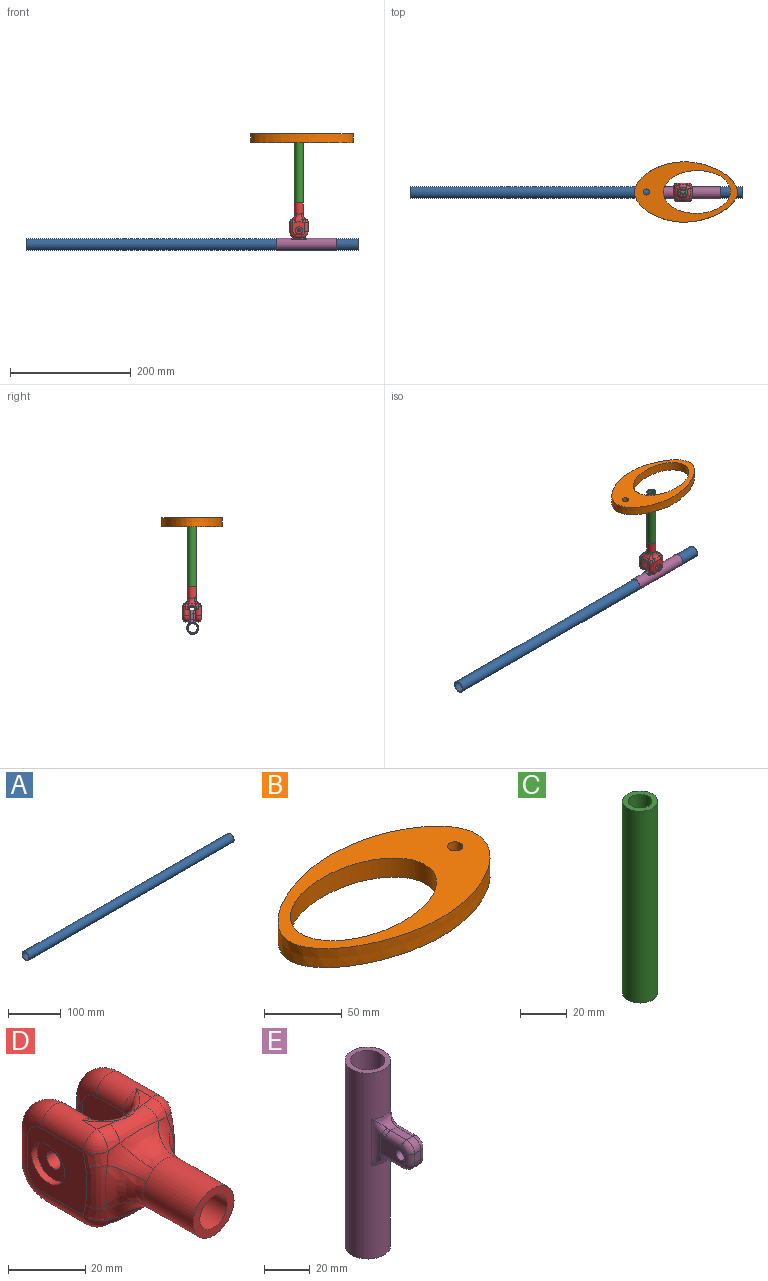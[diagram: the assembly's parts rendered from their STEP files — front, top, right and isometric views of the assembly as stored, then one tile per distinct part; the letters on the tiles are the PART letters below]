
ASSEMBLY  parts=5 mates=3
PART A: 4 faces, bbox 550x19x19 mm
  f0: cylinder r=8.5mm len=550mm, axis (-1,0,0), area 29373.9mm2, adj f2,f3
  f1: cylinder r=9.5mm len=550mm, axis (-1,0,0), area 32829.6mm2, adj f2,f3
  f2: plane 19x19mm, normal (1,0,0), area 56.5mm2, adj f0,f1
  f3: plane 19x19mm, normal (-1,0,0), area 56.5mm2, adj f0,f1
PART B: 5 faces, bbox 179.6x109.6x15 mm
  f0: extruded ~169.88x99.95mm, area 6393.3mm2, adj f1,f2
  f1: plane 179.64x109.64mm, normal (0,0,1), area 6702mm2, adj f0,f3,f4
  f2: plane 179.64x109.64mm, normal (0,0,-1), area 6702mm2, adj f0,f3,f4
  f3: extruded ~110.97x70.98mm, area 4340.2mm2, adj f1,f2
  f4: cylinder r=5mm len=15mm, axis (0,0,1), area 471.2mm2, adj f1,f2
PART C: 4 faces, bbox 15x15x100 mm
  f0: cylinder r=7.5mm len=100mm, axis (0,0,-1), area 4712.4mm2, adj f1,f2
  f1: plane 15x15mm, normal (0,0,1), area 98.2mm2, adj f0,f3
  f2: plane 15x15mm, normal (0,0,-1), area 98.2mm2, adj f0,f3
  f3: cylinder r=5mm len=100mm, axis (0,0,-1), area 3141.6mm2, adj f1,f2
PART D: 69 faces, bbox 33.5x59.8x50.3 mm
  f0: cylinder r=2.5mm len=8mm, axis (-1,0,0), area 125.7mm2, adj f9,f68
  f1: cylinder r=2.5mm len=8mm, axis (-1,0,0), area 125.7mm2, adj f10,f66
  f2: plane 8x7.58mm, normal (0,0,1), area 13.9mm2, adj f29,f40,f42,f64
  f3: plane 8x7.58mm, normal (0,0,-1), area 13.9mm2, adj f28,f37,f39,f58
  f4: plane 2.98x0.91mm, normal (0,1,0), area 0.9mm2, adj f46,f50,f62
  f5: plane 8x7.58mm, normal (0,0,1), area 13.9mm2, adj f24,f38,f40,f60
  f6: plane 8x7.58mm, normal (0,0,-1), area 13.9mm2, adj f23,f35,f37,f55
  f7: plane 21.69x20mm, normal (-1,0,0), area 300.7mm2, adj f23,f24,f25,f26,f27,f33,f34,f36
  f8: plane 21.69x20mm, normal (1,0,0), area 300.7mm2, adj f28,f29,f30,f31,f32,f41,f43,f44
  f9: plane 20x15mm, normal (-1,0,0), area 269.6mm2, adj f0,f28,f29,f30,f31,f32,f47,f49
  f10: plane 20x15mm, normal (1,0,0), area 269.6mm2, adj f1,f23,f24,f25,f26,f27,f47,f49
  f11: plane 2.98x0.91mm, normal (0,1,0), area 0.9mm2, adj f45,f48,f57
  f12: cylinder r=7.5mm len=18mm, axis (0,1,0), area 848.2mm2, adj f13,f14,f15,f16,f17,f18,f19,f20
  f13: plane 15x15mm, normal (0,-1,0), area 98.2mm2, adj f12,f22
  f14: bspline ~20.33x10.71mm, area 103.8mm2, adj f12,f15,f16,f34
  f15: torus R=17.5mm, axis (0,1,0), area 61.1mm2, adj f12,f14,f17,f33,f35
  f16: torus R=17.5mm, axis (0,1,0), area 61.1mm2, adj f12,f14,f18,f36,f38
  f17: bspline ~20.33x10.71mm, area 103.8mm2, adj f12,f15,f19,f37
  f18: bspline ~20.33x10.71mm, area 103.8mm2, adj f12,f16,f20,f40
  f19: torus R=17.5mm, axis (0,1,0), area 61.1mm2, adj f12,f17,f21,f39,f41
  f20: torus R=17.5mm, axis (0,1,0), area 61.1mm2, adj f12,f18,f21,f42,f44
  f21: bspline ~20.33x10.71mm, area 103.8mm2, adj f12,f19,f20,f43
  f22: cylinder r=5mm len=38mm, axis (0,-1,0), area 1193.8mm2, adj f13,f47,f49
  f23: cylinder r=5mm len=15.38mm, axis (0,-1,0), area 199.3mm2, adj f6,f7,f10,f25,f45,f51
  f24: cylinder r=5mm len=15.38mm, axis (0,1,0), area 199.3mm2, adj f5,f7,f10,f26,f46,f52
  f25: torus R=5mm, axis (-1,0,0), area 201.9mm2, adj f7,f10,f23,f27
  f26: torus R=5mm, axis (-1,0,0), area 201.9mm2, adj f7,f10,f24,f27
  f27: cylinder r=5mm len=10mm, axis (0,0,-1), area 157.1mm2, adj f7,f10,f25,f26
  f28: cylinder r=5mm len=15.38mm, axis (0,1,0), area 199.3mm2, adj f3,f8,f9,f30,f48,f53
  f29: cylinder r=5mm len=15.38mm, axis (0,-1,0), area 199.3mm2, adj f2,f8,f9,f31,f50,f54
  f30: torus R=5mm, axis (-1,0,0), area 201.9mm2, adj f8,f9,f28,f32
  f31: torus R=5mm, axis (-1,0,0), area 201.9mm2, adj f8,f9,f29,f32
  f32: cylinder r=5mm len=10mm, axis (0,0,1), area 157.1mm2, adj f8,f9,f30,f31
  f33: bspline ~8.9x6.01mm, area 25.9mm2, adj f7,f15,f34,f51
  f34: bspline ~14.38x4.87mm, area 72.5mm2, adj f7,f14,f33,f36
  f35: bspline ~8.9x6.01mm, area 25.9mm2, adj f6,f15,f37,f51
  f36: bspline ~8.9x6.01mm, area 25.9mm2, adj f7,f16,f34,f52
  f37: bspline ~14.38x4.87mm, area 70.7mm2, adj f3,f6,f17,f35,f39,f56,f57,f59
  f38: bspline ~8.9x6.01mm, area 25.9mm2, adj f5,f16,f40,f52
  f39: bspline ~8.9x6.01mm, area 25.9mm2, adj f3,f19,f37,f53
  f40: bspline ~14.43x4.88mm, area 70.7mm2, adj f2,f5,f18,f38,f42,f61,f62,f63
  f41: bspline ~8.9x6.01mm, area 25.9mm2, adj f8,f19,f43,f53
  f42: bspline ~8.9x6.01mm, area 25.9mm2, adj f2,f20,f40,f54
  f43: bspline ~14.43x4.88mm, area 72.5mm2, adj f8,f21,f41,f44
  f44: bspline ~8.9x6.01mm, area 25.9mm2, adj f8,f20,f43,f54
  f45: torus R=10mm, axis (0,-1,0), area 35.8mm2, adj f11,f23,f47,f55,f56
  f46: torus R=10mm, axis (0,-1,0), area 35.8mm2, adj f4,f24,f49,f60,f61
  f47: cylinder r=5mm len=10mm, axis (0,0,-1), area 107.1mm2, adj f9,f10,f22,f45,f48
  f48: torus R=10mm, axis (0,-1,0), area 35.8mm2, adj f11,f28,f47,f58,f59
  f49: cylinder r=5mm len=10mm, axis (0,0,-1), area 107.1mm2, adj f9,f10,f22,f46,f50
  f50: torus R=10mm, axis (0,-1,0), area 35.8mm2, adj f4,f29,f49,f63,f64
  f51: sphere r=5mm, area 50.9mm2, adj f23,f33,f35
  f52: sphere r=5mm, area 32.4mm2, adj f24,f36,f38
  f53: sphere r=5mm, area 32.4mm2, adj f28,f39,f41
  f54: sphere r=5mm, area 18.8mm2, adj f29,f42,f44
  f55: bspline ~7.97x6.73mm, area 9.8mm2, adj f6,f45,f56
  f56: bspline ~3.29x2.6mm, area 7mm2, adj f37,f45,f55,f57
  f57: bspline ~4.59x2.26mm, area 3.1mm2, adj f11,f37,f56,f59
  f58: bspline ~7.97x6.73mm, area 9.8mm2, adj f3,f48,f59
  f59: bspline ~3.29x2.6mm, area 7mm2, adj f37,f48,f57,f58
  f60: bspline ~7.97x6.73mm, area 9.8mm2, adj f5,f46,f61
  f61: bspline ~3.29x2.6mm, area 7mm2, adj f40,f46,f60,f62
  f62: bspline ~4.59x2.26mm, area 3.1mm2, adj f4,f40,f61,f63
  f63: bspline ~3.29x2.6mm, area 7mm2, adj f40,f50,f62,f64
  f64: bspline ~7.97x6.73mm, area 9.8mm2, adj f2,f50,f63
  f65: cylinder r=6mm len=12mm, axis (-1,0,0), area 75.4mm2, adj f7,f66
  f66: plane 12x12mm, normal (-1,0,0), area 93.5mm2, adj f1,f65
  f67: cylinder r=6mm len=12mm, axis (1,0,0), area 75.4mm2, adj f8,f68
  f68: plane 12x12mm, normal (1,0,0), area 93.5mm2, adj f0,f67
PART E: 34 faces, bbox 26.8x40x100 mm
  f0: cylinder r=10mm len=100mm, axis (0,0,-1), area 5916.2mm2, adj f1,f2,f8,f9,f10,f11
  f1: plane 20x20mm, normal (0,0,1), area 137.4mm2, adj f0,f14
  f2: plane 20x20mm, normal (0,0,-1), area 137.4mm2, adj f0,f14
  f3: plane 14.94x10.09mm, normal (-1,0,0), area 114.1mm2, adj f11,f16,f17,f18,f19,f20,f21,f22
  f4: plane 16.9x11.69mm, normal (1,0,0), area 134.6mm2, adj f8,f25,f26,f27,f28,f29,f30,f31
  f5: plane 10.32x4mm, normal (0,0,-1), area 40.3mm2, adj f10,f12,f17,f26
  f6: plane 10.32x4mm, normal (0,0,1), area 40.3mm2, adj f9,f13,f21,f30
  f7: plane 5x4mm, normal (0,-1,0), area 20mm2, adj f12,f13,f19,f28
  f8: cylinder r=5mm len=25mm, axis (0,0,-1), area 64.5mm2, adj f0,f4,f24,f32
  f9: torus R=15mm, axis (0,0,1), area 55.6mm2, adj f0,f6,f22,f23,f31,f32
  f10: torus R=15mm, axis (0,0,1), area 55.6mm2, adj f0,f5,f15,f16,f24,f25
  f11: cylinder r=5mm len=25mm, axis (0,0,-1), area 75.1mm2, adj f0,f3,f15,f23
  f12: cylinder r=5mm len=5mm, axis (-1,0,0), area 31.4mm2, adj f5,f7,f18,f27
  f13: cylinder r=5mm len=5mm, axis (1,0,0), area 31.4mm2, adj f6,f7,f20,f29
  f14: cylinder r=7.5mm len=100mm, axis (0,0,1), area 4712.4mm2, adj f1,f2
  f15: bspline ~7.83x5.89mm, area 20.2mm2, adj f10,f11,f16
  f16: bspline ~4.96x3.41mm, area 10.6mm2, adj f3,f10,f15,f17
  f17: cylinder r=3mm len=10.03mm, axis (0,1,0), area 47.3mm2, adj f3,f5,f16,f18
  f18: torus R=2mm, axis (1,0,0), area 28.9mm2, adj f3,f12,f17,f19
  f19: cylinder r=3mm len=5mm, axis (0,0,1), area 23.6mm2, adj f3,f7,f18,f20
  f20: torus R=2mm, axis (1,0,0), area 28.9mm2, adj f3,f13,f19,f21
  f21: cylinder r=3mm len=10.03mm, axis (0,-1,0), area 47.3mm2, adj f3,f6,f20,f22
  f22: bspline ~5.67x3.62mm, area 10.6mm2, adj f3,f9,f21,f23
  f23: bspline ~7.45x5.11mm, area 20.2mm2, adj f9,f11,f22
  f24: bspline ~6.66x4.96mm, area 15.6mm2, adj f8,f10,f25
  f25: bspline ~7.21x4.19mm, area 17mm2, adj f4,f10,f24,f26
  f26: cylinder r=3mm len=10.32mm, axis (0,-1,0), area 48.6mm2, adj f4,f5,f25,f27
  f27: torus R=2mm, axis (1,0,0), area 28.9mm2, adj f4,f12,f26,f28
  f28: cylinder r=3mm len=5mm, axis (0,0,-1), area 23.6mm2, adj f4,f7,f27,f29
  f29: torus R=2mm, axis (1,0,0), area 28.9mm2, adj f4,f13,f28,f30
  f30: cylinder r=3mm len=10.32mm, axis (0,1,0), area 48.6mm2, adj f4,f6,f29,f31
  f31: bspline ~7.21x4.19mm, area 17mm2, adj f4,f9,f30,f32
  f32: bspline ~6.66x4.96mm, area 15.6mm2, adj f8,f9,f31
  f33: cylinder r=2.5mm len=10mm, axis (1,0,0), area 157.1mm2, adj f3,f4
PLACE A rot(axis=(0,0,1),180deg) t=(104.27,-0.52,-111.27)mm
PLACE B rot(axis=(0,1,0),180deg) t=(6.46,0.26,72.8)mm
PLACE C t=(6.46,0.26,-42.2)mm
PLACE D rot(axis=(-0.58,0.58,-0.58),120deg) t=(-8.54,15.26,-70.2)mm
PLACE E rot(axis=(-0.58,-0.58,0.58),120deg) t=(68.96,-0.82,-110.43)mm
MATE parallel E.f7 <-> D.f12  axis (0,0,1) through (6.46,0.26,-80.43)mm
MATE parallel D.f12 <-> C.f0  axis (0,0,1) through (6.46,0.26,-42.2)mm
MATE parallel A.f0 <-> E.f0  axis (1,0,0) through (-445.73,-0.52,-111.27)mm
